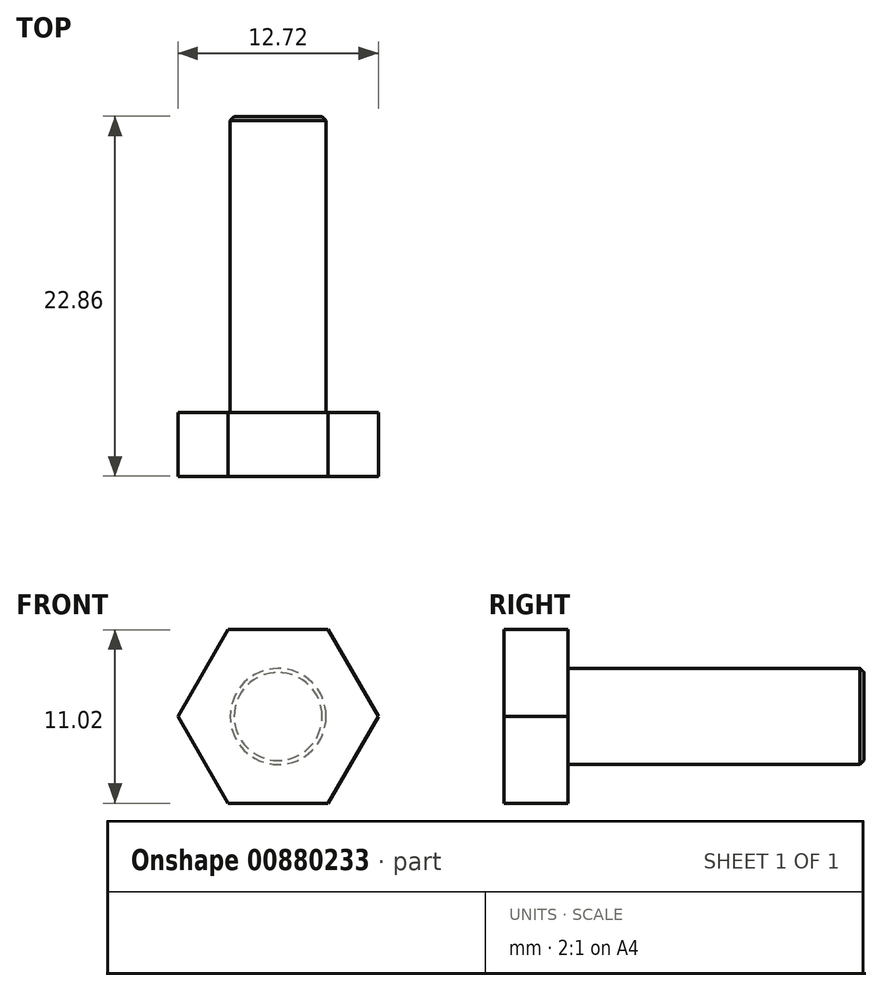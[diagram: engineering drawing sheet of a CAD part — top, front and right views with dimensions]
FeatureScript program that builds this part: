
annotation { "Feature Type Name" : "Feature", "Feature Type Description" : "" }
export const myFeature = defineFeature(function(context is Context, id is Id, definition is map)
    precondition{}
    {
        {
            var Q0;
            Q0=qCreatedBy(makeId("Front.planeOp"),FACE);
            var sketch = newSketch(context, id + "F0", { "sketchPlane" : qUnion([Q0])});
            skCircle(sketch, "E0.cCircle", {"center": v(0, 0) * mm, "radius": 5.51 * mm, "construction": true});
            skLineSegment(sketch, "E0.0", {"start": v(-3.18, 5.51) * mm, "end": v(3.18, 5.51) * mm});
            skLineSegment(sketch, "E0.1", {"start": v(3.18, 5.51) * mm, "end": v(6.36, 0) * mm});
            skLineSegment(sketch, "E0.2", {"start": v(6.36, 0) * mm, "end": v(3.18, -5.51) * mm});
            skLineSegment(sketch, "E0.3", {"start": v(3.18, -5.51) * mm, "end": v(-3.18, -5.51) * mm});
            skLineSegment(sketch, "E0.4", {"start": v(-3.18, -5.51) * mm, "end": v(-6.36, 0) * mm});
            skLineSegment(sketch, "E0.5", {"start": v(-6.36, 0) * mm, "end": v(-3.18, 5.51) * mm});
            skPoint(sketch, "E0.0.midPoint", {"position": v(0, 5.51) * mm});
            skSolve(sketch);
        }
        {
            var Q0;
            Q0=qSketchRegion(id+"F0",true);
            extrude(context, id + "F1", {"entities" : qUnion([Q0]), "depth" : 4.06 * mm});
        }
        {
            var Q0;
            Q0=makeQuery(id+"F1.opExtrude","CAP_FACE",FACE,{"disambiguationData":[OSD([sQuery(id+"F0.wireOp",EDGE,"E0.0"),sQuery(id+"F0.wireOp",EDGE,"E0.1"),sQuery(id+"F0.wireOp",EDGE,"E0.2"),sQuery(id+"F0.wireOp",EDGE,"E0.3"),sQuery(id+"F0.wireOp",EDGE,"E0.4"),sQuery(id+"F0.wireOp",EDGE,"E0.5")])],"isStart":true});
            var sketch = newSketch(context, id + "F2", { "sketchPlane" : qUnion([Q0])});
            skCircle(sketch, "E1", {"center": v(0, 0) * mm, "radius": 3.05 * mm});
            skSolve(sketch);
        }
        {
            var Q0;
            Q0=qSketchRegion(id+"F2",true);
            extrude(context, id + "F3", {"entities" : qUnion([Q0]), "operationType" : NewBodyOperationType.ADD, "depth" : 18.8 * mm});
        }
        {
            var Q0;
            Q0=makeQuery(id+"F3.opExtrude","CAP_EDGE",EDGE,{"disambiguationData":[OSD([sQuery(id+"F2.wireOp",EDGE,"E1")])],"isStart":false});
            chamfer(context, id + "F4", {"entities" : qUnion([Q0]), "width" : 0.25 * mm, "tangentPropagation" : true});
        }
    });
